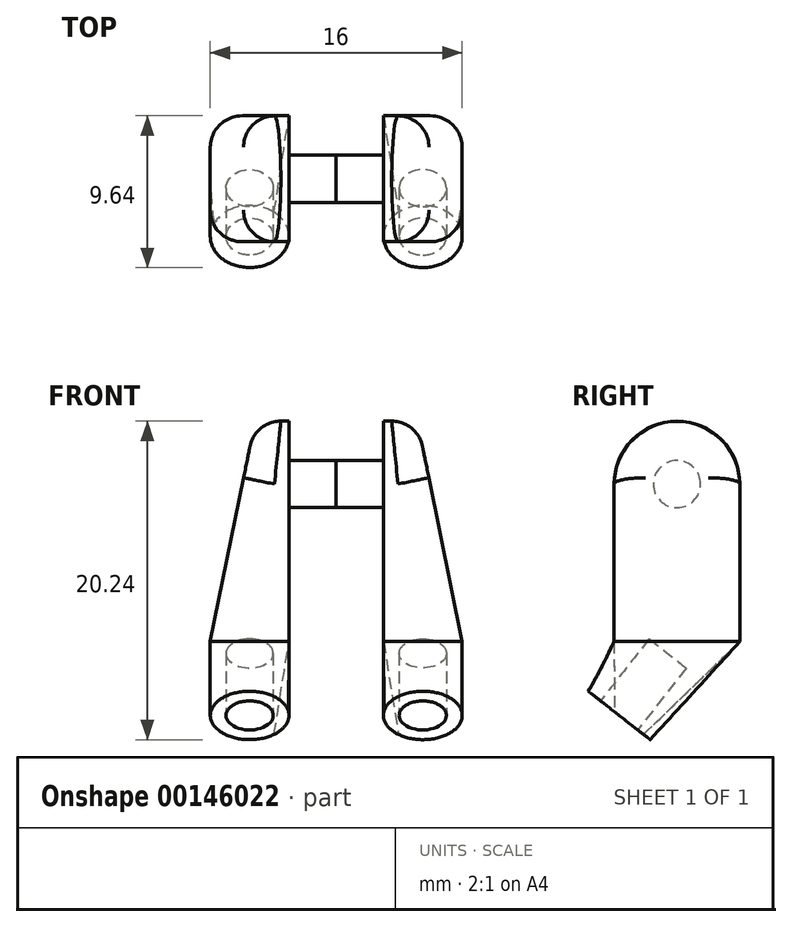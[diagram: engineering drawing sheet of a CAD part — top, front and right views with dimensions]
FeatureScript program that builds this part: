
annotation { "Feature Type Name" : "Feature", "Feature Type Description" : "" }
export const myFeature = defineFeature(function(context is Context, id is Id, definition is map)
    precondition{}
    {
        {
            var Q0;
            Q0=qCreatedBy(makeId("Right.planeOp"),FACE);
            var sketch = newSketch(context, id + "F0", { "sketchPlane" : qUnion([Q0])});
            skCircle(sketch, "E0", {"center": v(0, 0) * mm, "radius": 1.5 * mm});
            skSolve(sketch);
        }
        {
            var Q0;
            Q0=qSketchRegion(id+"F0",true);
            extrude(context, id + "F1", {"entities" : qUnion([Q0]), "depth" : 3 * mm});
        }
        {
            var Q0;
            Q0=makeQuery(id+"F1.opExtrude","CAP_FACE",FACE,{"disambiguationData":[OSD([sQuery(id+"F0.wireOp",EDGE,"E0")])],"isStart":false});
            var sketch = newSketch(context, id + "F2", { "sketchPlane" : qUnion([Q0])});
            skArc(sketch, "E1", {"start": v(4, 0) * mm, "mid": v(0, 4) * mm, "end": v(-4, 0) * mm});
            skLineSegment(sketch, "E2.top", {"start": v(4, -10) * mm, "end": v(-4, -10) * mm});
            skLineSegment(sketch, "E2.left", {"start": v(4, 0) * mm, "end": v(4, -10) * mm});
            skLineSegment(sketch, "E2.right", {"start": v(-4, 0) * mm, "end": v(-4, -10) * mm});
            skPoint(sketch, "E2.middle", {"position": v(0, -5) * mm});
            skLineSegment(sketch, "E3", {"start": v(4, -10) * mm, "end": v(-1.19, -16.64) * mm, "construction": true});
            skLineSegment(sketch, "E4", {"start": v(-1.19, -16.64) * mm, "end": v(-6.15, -12.76) * mm, "construction": true});
            skLineSegment(sketch, "E5", {"start": v(-6.15, -12.76) * mm, "end": v(-4, -10) * mm, "construction": true});
            skLineSegment(sketch, "E6", {"start": v(-3.67, -14.7) * mm, "end": v(-1.83, -12.34) * mm, "construction": true});
            skSolve(sketch);
        }
        {
            var Q0;
            Q0=qSketchRegion(id+"F2",true);
            extrude(context, id + "F3", {"entities" : qUnion([Q0]), "operationType" : NewBodyOperationType.ADD, "depth" : 5 * mm});
        }
        {
            var Q0;
            Q0=makeQuery(id+"F3.opExtrude","SWEPT_FACE",FACE,{"disambiguationData":[OSD([sQuery(id+"F2.wireOp",EDGE,"E2.right")])]});
            var sketch = newSketch(context, id + "F4", { "sketchPlane" : qUnion([Q0])});
            skLineSegment(sketch, "E7", {"start": v(8, -10) * mm, "end": v(4.6, 6.67) * mm});
            skLineSegment(sketch, "E8", {"start": v(4.6, 6.67) * mm, "end": v(11.64, 6.67) * mm});
            skLineSegment(sketch, "E9", {"start": v(11.64, 6.67) * mm, "end": v(8, -10) * mm});
            skSolve(sketch);
        }
        {
            var Q0;
            Q0=qSketchRegion(id+"F4",true);
            extrude(context, id + "F5", {"entities" : qUnion([Q0]), "operationType" : NewBodyOperationType.REMOVE, "oppositeDirection" : true, "depth" : 25 * mm});
        }
        {
            var Q0;
            Q0=makeQuery(id+"F5.boolean.opBoolean","INTERSECT",EDGE,{"derivedFrom":[makeQuery(id+"F3.opExtrude","SWEPT_FACE",FACE,{"disambiguationData":[OSD([sQuery(id+"F2.wireOp",EDGE,"E1")])]}),makeQuery(id+"F5.opExtrude","SWEPT_FACE",FACE,{"disambiguationData":[OSD([sQuery(id+"F4.wireOp",EDGE,"E7")])]})]});
            var Q1;
            Q1=makeQuery(id+"F5.boolean.opBoolean","INTERSECT",EDGE,{"derivedFrom":[makeQuery(id+"F3.opExtrude","SWEPT_FACE",FACE,{"disambiguationData":[OSD([sQuery(id+"F2.wireOp",EDGE,"E2.left")])]}),makeQuery(id+"F5.opExtrude","SWEPT_FACE",FACE,{"disambiguationData":[OSD([sQuery(id+"F4.wireOp",EDGE,"E7")])]})]});
            var Q2;
            Q2=makeQuery(id+"F5.boolean.opBoolean","COPY",EDGE,{"derivedFrom":makeQuery(id+"F5.opExtrude","CAP_EDGE",EDGE,{"disambiguationData":[OSD([sQuery(id+"F4.wireOp",EDGE,"E7")])],"isStart":true})});
            fillet(context, id + "F6", {"entities" : qUnion([Q0, Q1, Q2]), "radius" : 2 * mm, "tangentPropagation" : true, "allowEdgeOverflow" : false});
        }
        {
            var Q0;
            Q0=sQuery(id+"F2.wireOp",VERTEX,"E5.start");
            var Q1;
            Q1=sQuery(id+"F2.wireOp",EDGE,"E5");
            cPlane(context, id + "F7", {"entities" : qUnion([Q0, Q1]), "cplaneType" : CPlaneType.LINE_POINT, "offset" : 150 * mm, "width" : 150 * mm, "height" : 150 * mm});
        }
        {
            var Q0;
            Q0=qCreatedBy(id+"F7.planeOp",FACE);
            var sketch = newSketch(context, id + "F8", { "sketchPlane" : qUnion([Q0])});
            skLineSegment(sketch, "E10", {"start": v(3, 6.16) * mm, "end": v(9.15, 6.16) * mm, "construction": true});
            skCircle(sketch, "E11", {"center": v(5.5, 6.16) * mm, "radius": 2.5 * mm});
            skSolve(sketch);
        }
        {
            var Q1;
            Q1=makeQuery(id+"F3.opExtrude","SWEPT_FACE",FACE,{"disambiguationData":[OSD([sQuery(id+"F2.wireOp",EDGE,"E2.top")])]});
            var Q2;
            Q2=makeQuery(id+"F8.imprint","IMPRINT",FACE,{"disambiguationData":[TD([[makeQuery(id+"F8.imprint","IMPRINT",EDGE,{"derivedFrom":sQuery(id+"F8.wireOp",EDGE,"E11")}),1.0]])]});
            loft(context, id + "F9", {"operationType" : NewBodyOperationType.ADD, "sheetProfilesArray" : [{ "sheetProfileEntities" : qUnion([Q1]) }, { "sheetProfileEntities" : qUnion([Q2]) }]});
        }
        {
            var Q0;
            Q0=makeQuery(id+"F8.imprint","IMPRINT",FACE,{"disambiguationData":[TD([[makeQuery(id+"F8.imprint","IMPRINT",EDGE,{"derivedFrom":sQuery(id+"F8.wireOp",EDGE,"E11")}),1.0]])]});
            var sketch = newSketch(context, id + "F10", { "sketchPlane" : qUnion([Q0])});
            skCircle(sketch, "E12", {"center": v(5.5, 6.16) * mm, "radius": 1.5 * mm});
            skSolve(sketch);
        }
        {
            var Q0;
            Q0=qSketchRegion(id+"F10",true);
            extrude(context, id + "F11", {"entities" : qUnion([Q0]), "operationType" : NewBodyOperationType.REMOVE, "depth" : 5 * mm});
        }
        {
            var Q0;
            Q0=makeQuery(id+"F1.opExtrude","SWEPT_BODY",BODY,{"disambiguationData":[OSD([sQuery(id+"F0.wireOp",EDGE,"E0")])]});
            var Q1;
            Q1=makeQuery(id+"F1.opExtrude","CAP_FACE",FACE,{"disambiguationData":[OSD([sQuery(id+"F0.wireOp",EDGE,"E0")])],"isStart":true});
            mirror(context, id + "F12", {"entities" : qUnion([Q0]), "mirrorPlane" : qUnion([Q1])});
        }
    });
